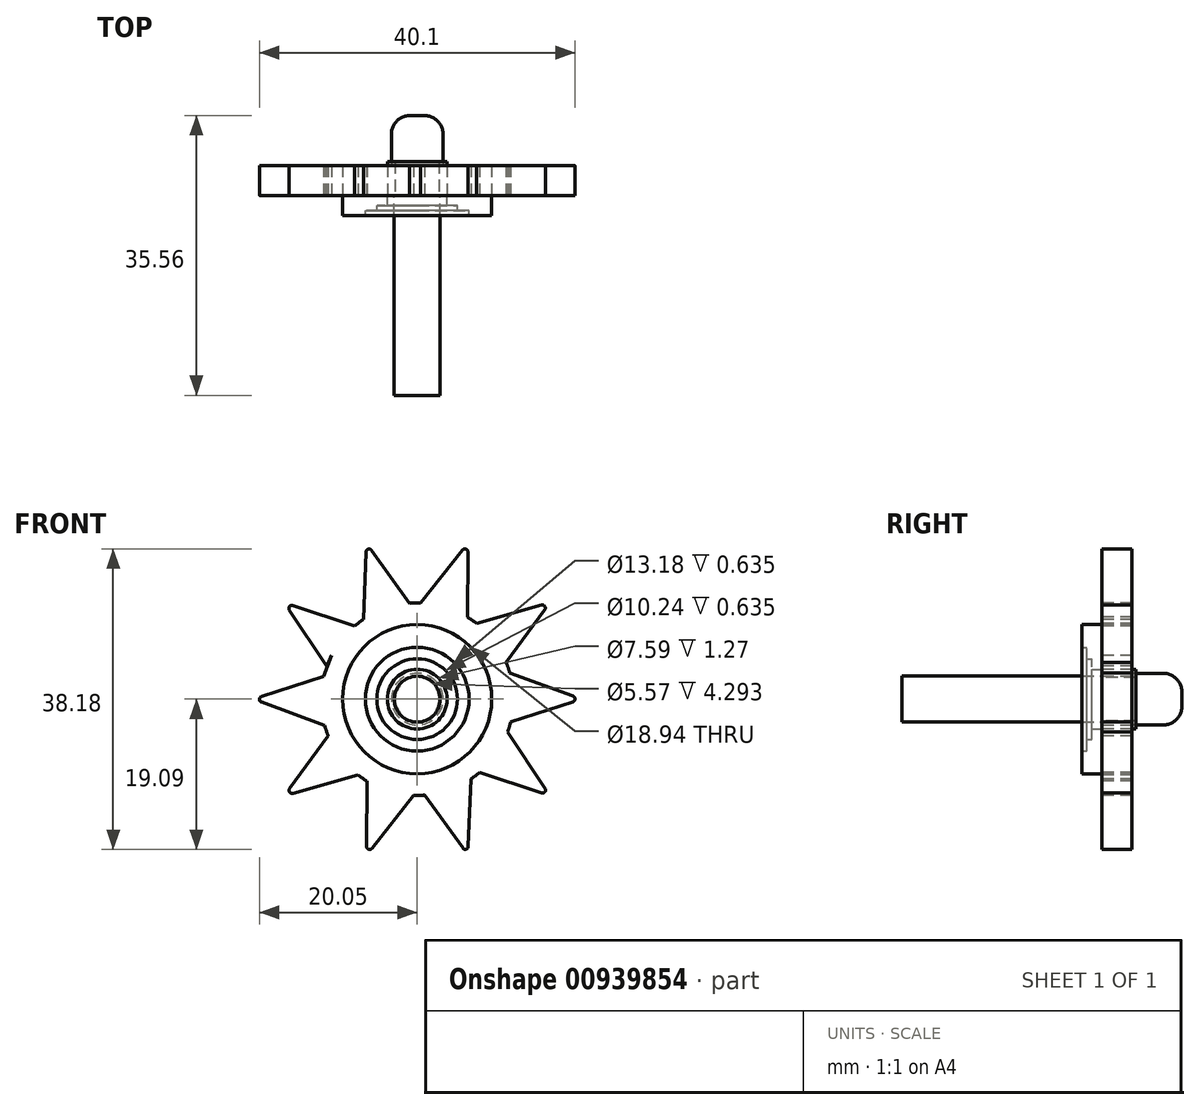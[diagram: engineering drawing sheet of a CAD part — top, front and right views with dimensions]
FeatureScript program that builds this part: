
annotation { "Feature Type Name" : "Feature", "Feature Type Description" : "" }
export const myFeature = defineFeature(function(context is Context, id is Id, definition is map)
    precondition{}
    {
        {
            var Q0;
            Q0=qCreatedBy(makeId("Front.planeOp"),FACE);
            var sketch = newSketch(context, id + "F0", { "sketchPlane" : qUnion([Q0])});
            skCircle(sketch, "E0", {"center": v(0, 0) * mm, "radius": 12.22 * mm});
            skCircle(sketch, "E1", {"center": v(0, 0) * mm, "radius": 9.47 * mm});
            skCircle(sketch, "E2", {"center": v(0, 0) * mm, "radius": 6.59 * mm});
            skCircle(sketch, "E3", {"center": v(0, 0) * mm, "radius": 5.12 * mm});
            skCircle(sketch, "E4", {"center": v(0, 0) * mm, "radius": 3.8 * mm});
            skCircle(sketch, "E5", {"center": v(0, 0) * mm, "radius": 2.79 * mm});
            skCircle(sketch, "E6", {"center": v(0, 0) * mm, "radius": 1.84 * mm});
            skLineSegment(sketch, "E7", {"start": v(-11.75, -3.36) * mm, "end": v(-20.83, 0) * mm});
            skLineSegment(sketch, "E8", {"start": v(-20.83, 0) * mm, "end": v(-11.88, 2.87) * mm});
            skLineSegment(sketch, "E9", {"start": v(-11.88, 2.87) * mm, "end": v(-10.89, 5.55) * mm});
            skLineSegment(sketch, "E10.1.0", {"start": v(-16.86, -12.25) * mm, "end": v(-11.3, -4.67) * mm});
            skLineSegment(sketch, "E10.1.1", {"start": v(-7.54, -9.62) * mm, "end": v(-16.86, -12.25) * mm});
            skLineSegment(sketch, "E10.2.0", {"start": v(-6.44, -19.81) * mm, "end": v(-6.4, -10.41) * mm});
            skLineSegment(sketch, "E10.2.1", {"start": v(-0.44, -12.22) * mm, "end": v(-6.44, -19.81) * mm});
            skLineSegment(sketch, "E10.3.0", {"start": v(6.44, -19.81) * mm, "end": v(0.95, -12.19) * mm});
            skLineSegment(sketch, "E10.3.1", {"start": v(6.82, -10.14) * mm, "end": v(6.44, -19.81) * mm});
            skLineSegment(sketch, "E10.4.0", {"start": v(16.86, -12.25) * mm, "end": v(7.93, -9.3) * mm});
            skLineSegment(sketch, "E10.4.1", {"start": v(11.48, -4.2) * mm, "end": v(16.86, -12.25) * mm});
            skLineSegment(sketch, "E10.5.0", {"start": v(20.83, 0) * mm, "end": v(11.88, -2.87) * mm});
            skLineSegment(sketch, "E10.5.1", {"start": v(11.75, 3.36) * mm, "end": v(20.83, 0) * mm});
            skLineSegment(sketch, "E11.1.6.0", {"start": v(16.86, 12.25) * mm, "end": v(11.3, 4.67) * mm});
            skLineSegment(sketch, "E11.3.6.0", {"start": v(7.54, 9.62) * mm, "end": v(16.86, 12.25) * mm});
            skLineSegment(sketch, "E11.1.7.0", {"start": v(6.44, 19.81) * mm, "end": v(6.4, 10.41) * mm});
            skLineSegment(sketch, "E11.3.7.0", {"start": v(0.44, 12.22) * mm, "end": v(6.44, 19.81) * mm});
            skLineSegment(sketch, "E11.1.8.0", {"start": v(-6.44, 19.81) * mm, "end": v(-0.95, 12.19) * mm});
            skLineSegment(sketch, "E11.3.8.0", {"start": v(-6.82, 10.14) * mm, "end": v(-6.44, 19.81) * mm});
            skLineSegment(sketch, "E11.1.9.0", {"start": v(-16.86, 12.25) * mm, "end": v(-7.93, 9.3) * mm});
            skLineSegment(sketch, "E11.3.9.0", {"start": v(-11.48, 4.2) * mm, "end": v(-16.86, 12.25) * mm});
            skSolve(sketch);
        }
        {
            var Q0;
            {var subQ0=sQuery(id+"F0.wireOp",EDGE,"E10.5.0");Q0=makeQuery(id+"F0.imprint","IMPRINT",FACE,{"disambiguationData":[TD([[makeQuery(id+"F0.imprint","IMPRINT",EDGE,{"derivedFrom":subQ0}),-1.0]])]});}
            var Q1;
            {var subQ0=sQuery(id+"F0.wireOp",EDGE,"E11.1.6.0");Q1=makeQuery(id+"F0.imprint","IMPRINT",FACE,{"disambiguationData":[TD([[makeQuery(id+"F0.imprint","IMPRINT",EDGE,{"derivedFrom":subQ0}),-1.0]])]});}
            var Q2;
            {var subQ0=sQuery(id+"F0.wireOp",EDGE,"E11.1.8.0");Q2=makeQuery(id+"F0.imprint","IMPRINT",FACE,{"disambiguationData":[TD([[makeQuery(id+"F0.imprint","IMPRINT",EDGE,{"derivedFrom":subQ0}),-1.0]])]});}
            var Q3;
            {var subQ0=sQuery(id+"F0.wireOp",EDGE,"E11.1.7.0");Q3=makeQuery(id+"F0.imprint","IMPRINT",FACE,{"disambiguationData":[TD([[makeQuery(id+"F0.imprint","IMPRINT",EDGE,{"derivedFrom":subQ0}),-1.0]])]});}
            var Q4;
            {var subQ2=sQuery(id+"F0.wireOp",EDGE,"E11.1.9.0");Q4=makeQuery(id+"F0.imprint","IMPRINT",FACE,{"disambiguationData":[TD([[makeQuery(id+"F0.imprint","IMPRINT",EDGE,{"derivedFrom":subQ2}),-1.0]])]});}
            var Q5;
            {var subQ0=sQuery(id+"F0.wireOp",EDGE,"E7");Q5=makeQuery(id+"F0.imprint","IMPRINT",FACE,{"disambiguationData":[TD([[makeQuery(id+"F0.imprint","IMPRINT",EDGE,{"derivedFrom":subQ0}),-1.0]])]});}
            var Q6;
            {var subQ0=sQuery(id+"F0.wireOp",EDGE,"E10.1.0");Q6=makeQuery(id+"F0.imprint","IMPRINT",FACE,{"disambiguationData":[TD([[makeQuery(id+"F0.imprint","IMPRINT",EDGE,{"derivedFrom":subQ0}),-1.0]])]});}
            var Q7;
            {var subQ0=sQuery(id+"F0.wireOp",EDGE,"E10.2.0");Q7=makeQuery(id+"F0.imprint","IMPRINT",FACE,{"disambiguationData":[TD([[makeQuery(id+"F0.imprint","IMPRINT",EDGE,{"derivedFrom":subQ0}),-1.0]])]});}
            var Q8;
            {var subQ0=sQuery(id+"F0.wireOp",EDGE,"E10.3.0");Q8=makeQuery(id+"F0.imprint","IMPRINT",FACE,{"disambiguationData":[TD([[makeQuery(id+"F0.imprint","IMPRINT",EDGE,{"derivedFrom":subQ0}),-1.0]])]});}
            var Q9;
            {var subQ0=sQuery(id+"F0.wireOp",EDGE,"E10.4.0");Q9=makeQuery(id+"F0.imprint","IMPRINT",FACE,{"disambiguationData":[TD([[makeQuery(id+"F0.imprint","IMPRINT",EDGE,{"derivedFrom":subQ0}),-1.0]])]});}
            var Q10;
            Q10=makeQuery(id+"F0.imprint","IMPRINT",FACE,{"disambiguationData":[TD([[makeQuery(id+"F0.imprint","IMPRINT",EDGE,{"derivedFrom":sQuery(id+"F0.wireOp",EDGE,"E1")}),-1.0]])]});
            extrude(context, id + "F1", {"entities" : qUnion([Q0, Q1, Q2, Q3, Q4, Q5, Q6, Q7, Q8, Q9, Q10]), "oppositeDirection" : true, "depth" : 3.8 * mm, "offsetDistance" : 25.4 * mm});
        }
        {
            var Q0;
            Q0=makeQuery(id+"F1.opExtrude","CAP_FACE",FACE,{"disambiguationData":[OSD([sQuery(id+"F0.wireOp",EDGE,"E0"),sQuery(id+"F0.wireOp",EDGE,"E7"),sQuery(id+"F0.wireOp",EDGE,"E8"),sQuery(id+"F0.wireOp",EDGE,"E10.1.0"),sQuery(id+"F0.wireOp",EDGE,"E10.1.1"),sQuery(id+"F0.wireOp",EDGE,"E10.2.0"),sQuery(id+"F0.wireOp",EDGE,"E10.2.1"),sQuery(id+"F0.wireOp",EDGE,"E10.3.0"),sQuery(id+"F0.wireOp",EDGE,"E10.3.1"),sQuery(id+"F0.wireOp",EDGE,"E10.4.0"),sQuery(id+"F0.wireOp",EDGE,"E10.4.1"),sQuery(id+"F0.wireOp",EDGE,"E10.5.0"),sQuery(id+"F0.wireOp",EDGE,"E10.5.1")])],"isStart":true});
            var sketch = newSketch(context, id + "F2", { "sketchPlane" : qUnion([Q0])});
            skCircle(sketch, "E12", {"center": v(0, 0) * mm, "radius": 2.92 * mm});
            skSolve(sketch);
        }
        {
            var Q0;
            Q0 = qSketchRegion(id + "F2", true);
            extrude(context, id + "F3", {"entities" : qUnion([Q0]), "operationType" : NewBodyOperationType.ADD, "depth" : 25.4 * mm, "offsetDistance" : 25.4 * mm});
        }
        {
            var Q0;
            Q0=makeQuery(id+"F1.opExtrude","CAP_FACE",FACE,{"disambiguationData":[OSD([sQuery(id+"F0.wireOp",EDGE,"E0"),sQuery(id+"F0.wireOp",EDGE,"E7"),sQuery(id+"F0.wireOp",EDGE,"E8"),sQuery(id+"F0.wireOp",EDGE,"E10.1.0"),sQuery(id+"F0.wireOp",EDGE,"E10.1.1"),sQuery(id+"F0.wireOp",EDGE,"E10.2.0"),sQuery(id+"F0.wireOp",EDGE,"E10.2.1"),sQuery(id+"F0.wireOp",EDGE,"E10.3.0"),sQuery(id+"F0.wireOp",EDGE,"E10.3.1"),sQuery(id+"F0.wireOp",EDGE,"E10.4.0"),sQuery(id+"F0.wireOp",EDGE,"E10.4.1"),sQuery(id+"F0.wireOp",EDGE,"E10.5.0"),sQuery(id+"F0.wireOp",EDGE,"E10.5.1")])],"isStart":false});
            var sketch = newSketch(context, id + "F4", { "sketchPlane" : qUnion([Q0])});
            skCircle(sketch, "E13", {"center": v(0, 0) * mm, "radius": 3.29 * mm});
            skSolve(sketch);
        }
        {
            var Q0;
            Q0 = qSketchRegion(id + "F4", true);
            extrude(context, id + "F5", {"entities" : qUnion([Q0]), "operationType" : NewBodyOperationType.ADD, "depth" : 6.35 * mm, "offsetDistance" : 25.4 * mm});
        }
        {
            var Q0;
            Q0=makeQuery(id+"F1.opExtrude","SWEPT_EDGE",EDGE,{"disambiguationData":[OSD([sQuery(id+"F0.wireOp",EDGE,"E7"),sQuery(id+"F0.wireOp",EDGE,"E8")])]});
            var Q1;
            Q1=makeQuery(id+"F1.opExtrude","SWEPT_EDGE",EDGE,{"disambiguationData":[OSD([sQuery(id+"F0.wireOp",EDGE,"E10.1.0"),sQuery(id+"F0.wireOp",EDGE,"E10.1.1")])]});
            var Q2;
            Q2=makeQuery(id+"F1.opExtrude","SWEPT_EDGE",EDGE,{"disambiguationData":[OSD([sQuery(id+"F0.wireOp",EDGE,"E10.2.0"),sQuery(id+"F0.wireOp",EDGE,"E10.2.1")])]});
            var Q3;
            Q3=makeQuery(id+"F1.opExtrude","SWEPT_EDGE",EDGE,{"disambiguationData":[OSD([sQuery(id+"F0.wireOp",EDGE,"E10.3.0"),sQuery(id+"F0.wireOp",EDGE,"E10.3.1")])]});
            var Q4;
            Q4=makeQuery(id+"F1.opExtrude","SWEPT_EDGE",EDGE,{"disambiguationData":[OSD([sQuery(id+"F0.wireOp",EDGE,"E10.4.0"),sQuery(id+"F0.wireOp",EDGE,"E10.4.1")])]});
            var Q5;
            Q5=makeQuery(id+"F1.opExtrude","SWEPT_EDGE",EDGE,{"disambiguationData":[OSD([sQuery(id+"F0.wireOp",EDGE,"E10.5.0"),sQuery(id+"F0.wireOp",EDGE,"E10.5.1")])]});
            var Q6;
            Q6=makeQuery(id+"F1.opExtrude","SWEPT_EDGE",EDGE,{"disambiguationData":[OSD([sQuery(id+"F0.wireOp",EDGE,"E11.1.6.0"),sQuery(id+"F0.wireOp",EDGE,"E11.3.6.0")])]});
            var Q7;
            Q7=makeQuery(id+"F1.opExtrude","SWEPT_EDGE",EDGE,{"disambiguationData":[OSD([sQuery(id+"F0.wireOp",EDGE,"E11.1.7.0"),sQuery(id+"F0.wireOp",EDGE,"E11.3.7.0")])]});
            var Q8;
            Q8=makeQuery(id+"F1.opExtrude","SWEPT_EDGE",EDGE,{"disambiguationData":[OSD([sQuery(id+"F0.wireOp",EDGE,"E11.1.8.0"),sQuery(id+"F0.wireOp",EDGE,"E11.3.8.0")])]});
            var Q9;
            Q9=makeQuery(id+"F1.opExtrude","SWEPT_EDGE",EDGE,{"disambiguationData":[OSD([sQuery(id+"F0.wireOp",EDGE,"E11.1.9.0"),sQuery(id+"F0.wireOp",EDGE,"E11.3.9.0")])]});
            fillet(context, id + "F6", {"entities" : qUnion([Q0, Q1, Q2, Q3, Q4, Q5, Q6, Q7, Q8, Q9]), "radius" : 0.38 * mm, "tangentPropagation" : true, "allowEdgeOverflow" : false});
        }
        {
            var Q0;
            Q0=makeQuery(id+"F0.imprint","IMPRINT",FACE,{"disambiguationData":[TD([[makeQuery(id+"F0.imprint","IMPRINT",EDGE,{"derivedFrom":sQuery(id+"F0.wireOp",EDGE,"E1")}),1.0]])]});
            extrude(context, id + "F7", {"entities" : qUnion([Q0]), "depth" : 2.54 * mm, "offsetDistance" : 25.4 * mm});
        }
        {
            var Q0;
            Q0=makeQuery(id+"F0.imprint","IMPRINT",FACE,{"disambiguationData":[TD([[makeQuery(id+"F0.imprint","IMPRINT",EDGE,{"derivedFrom":sQuery(id+"F0.wireOp",EDGE,"E2")}),1.0]])]});
            extrude(context, id + "F8", {"entities" : qUnion([Q0]), "operationType" : NewBodyOperationType.ADD, "depth" : 1.9 * mm, "offsetDistance" : 25.4 * mm});
        }
        {
            var Q0;
            Q0=makeQuery(id+"F0.imprint","IMPRINT",FACE,{"disambiguationData":[TD([[makeQuery(id+"F0.imprint","IMPRINT",EDGE,{"derivedFrom":sQuery(id+"F0.wireOp",EDGE,"E3")}),1.0]])]});
            extrude(context, id + "F9", {"entities" : qUnion([Q0]), "operationType" : NewBodyOperationType.ADD, "depth" : 1.27 * mm, "offsetDistance" : 25.4 * mm});
        }
        {
            var Q0;
            Q0=makeQuery(id+"F0.imprint","IMPRINT",FACE,{"disambiguationData":[TD([[makeQuery(id+"F0.imprint","IMPRINT",EDGE,{"derivedFrom":sQuery(id+"F0.wireOp",EDGE,"E4")}),1.0]])]});
            extrude(context, id + "F10", {"entities" : qUnion([Q0]), "oppositeDirection" : true, "depth" : 4.3 * mm, "offsetDistance" : 25.4 * mm});
        }
        {
            var Q0;
            Q0=makeQuery(id+"F5.opExtrude","CAP_FACE",FACE,{"disambiguationData":[OSD([sQuery(id+"F4.wireOp",EDGE,"E13")])],"isStart":false});
            fillet(context, id + "F11", {"entities" : qUnion([Q0]), "radius" : 2.4 * mm, "tangentPropagation" : true, "allowEdgeOverflow" : false});
        }
    });
